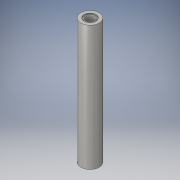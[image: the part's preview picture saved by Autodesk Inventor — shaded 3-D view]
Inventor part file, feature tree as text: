
AUTODESK INVENTOR PART (.ipt)
format: ipt  version: 2016 (Build 200138000, 138)  size: 122,368 bytes
history: native  units: in
note: dims shown in document units (in); Inventor stores cm internally (conversion verified against a paired STEP export)
features: extrude x5, sketch x5
ambient origin geometry x8: Origin, YZ Plane, XZ Plane, XY Plane, X Axis, Y Axis, Z Axis, Center Point
bodies: Solid1 (feature_tree)
feature tree (10):
  extrude  "Extrusion1"  Depth=12.013in TaperAngle=0.0deg
  extrude  "Extrusion2"  Depth=0.995in
  sketch  "Sketch3"  dims[d5=0.071in d6=0.0in d7=0.0666in]
  extrude  "Extrusion3"  Depth=0.071in
  extrude  "Extrusion4"  Depth=14.0in TaperAngle=0.0deg
  extrude  "Extrusion5"  Depth=11.435in
  sketch  "Sketch1"  dims[d0=1.748in d1=12.013in d2=0.0in]
  sketch  "Sketch2"  dims[d3=1.138in d4=0.995in]
  sketch  "Sketch5"  dims[d9=0.577in d10=-0.1168in d11=14.0in d12=0.0in]
  sketch  "Sketch6"  dims[d13=1.5in d14=1.748in d15=11.435in d16=0.0in]
